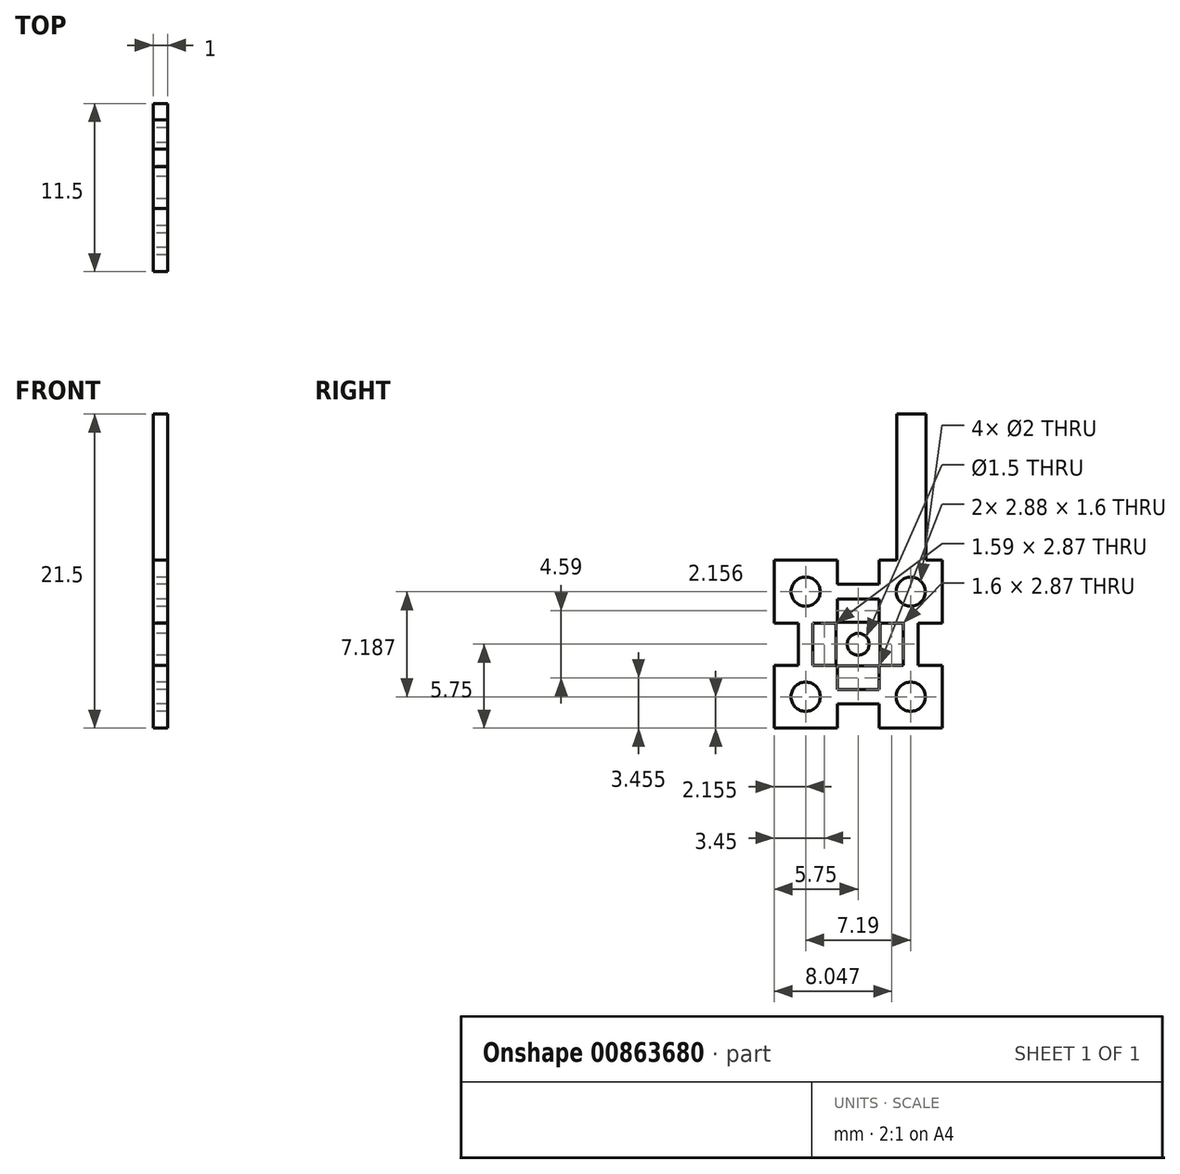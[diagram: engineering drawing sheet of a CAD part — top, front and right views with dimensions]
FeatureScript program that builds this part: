
annotation { "Feature Type Name" : "Feature", "Feature Type Description" : "" }
export const myFeature = defineFeature(function(context is Context, id is Id, definition is map)
    precondition{}
    {
        {
            var Q0;
            Q0=qCreatedBy(makeId("Right.planeOp"),FACE);
            var sketch = newSketch(context, id + "F0", { "sketchPlane" : qUnion([Q0])});
            skLineSegment(sketch, "E0.bottom", {"start": v(0, 0) * mm, "end": v(4.31, 0) * mm});
            skLineSegment(sketch, "E0.top", {"start": v(0, -11.5) * mm, "end": v(4.31, -11.5) * mm});
            skLineSegment(sketch, "E0.left", {"start": v(0, 0) * mm, "end": v(0, -4.31) * mm});
            skLineSegment(sketch, "E1", {"start": v(11.5, 0) * mm, "end": v(11.5, -4.31) * mm});
            skLineSegment(sketch, "E2", {"start": v(10.38, 0) * mm, "end": v(10.38, 10) * mm});
            skLineSegment(sketch, "E3", {"start": v(10.38, 10) * mm, "end": v(8.38, 10) * mm});
            skLineSegment(sketch, "E4", {"start": v(8.38, 10) * mm, "end": v(8.38, 0) * mm});
            skLineSegment(sketch, "E5.trimOffspring", {"start": v(10.38, 0) * mm, "end": v(11.5, 0) * mm});
            skLineSegment(sketch, "E6.0", {"start": v(0, -7.19) * mm, "end": v(4.31, -7.19) * mm});
            skLineSegment(sketch, "E7.0", {"start": v(0, -4.31) * mm, "end": v(4.31, -4.31) * mm});
            skLineSegment(sketch, "E8.0", {"start": v(4.31, 0) * mm, "end": v(4.31, -4.31) * mm});
            skLineSegment(sketch, "E9.0", {"start": v(7.19, 0) * mm, "end": v(7.19, -4.31) * mm});
            skLineSegment(sketch, "E10", {"start": v(8.38, 0) * mm, "end": v(7.19, 0) * mm});
            skLineSegment(sketch, "E11", {"start": v(7.19, 0) * mm, "end": v(8.38, 0) * mm});
            skLineSegment(sketch, "E12.trimOffspring", {"start": v(0, -7.19) * mm, "end": v(0, -11.5) * mm});
            skLineSegment(sketch, "E13.trimOffspring", {"start": v(4.31, -7.19) * mm, "end": v(4.31, -11.5) * mm});
            skLineSegment(sketch, "E14.trimOffspring", {"start": v(7.19, -7.19) * mm, "end": v(7.19, -11.5) * mm});
            skLineSegment(sketch, "E15.trimOffspring", {"start": v(11.5, -7.19) * mm, "end": v(11.5, -11.5) * mm});
            skLineSegment(sketch, "E16.trimOffspring", {"start": v(7.19, -4.31) * mm, "end": v(11.5, -4.31) * mm});
            skLineSegment(sketch, "E17.trimOffspring", {"start": v(7.19, -7.19) * mm, "end": v(11.5, -7.19) * mm});
            skLineSegment(sketch, "E18.trimOffspring", {"start": v(7.19, -11.5) * mm, "end": v(11.5, -11.5) * mm});
            skLineSegment(sketch, "E19.0", {"start": v(4.31, -2.66) * mm, "end": v(7.19, -2.66) * mm});
            skLineSegment(sketch, "E20.0", {"start": v(4.31, -1.66) * mm, "end": v(7.19, -1.66) * mm});
            skLineSegment(sketch, "E21.0", {"start": v(1.66, -4.31) * mm, "end": v(1.66, -7.19) * mm});
            skLineSegment(sketch, "E22.0", {"start": v(2.66, -4.31) * mm, "end": v(2.66, -7.19) * mm});
            skLineSegment(sketch, "E23.0", {"start": v(4.3, -9.84) * mm, "end": v(7.19, -9.84) * mm});
            skLineSegment(sketch, "E24.0", {"start": v(4.31, -8.84) * mm, "end": v(7.19, -8.84) * mm});
            skLineSegment(sketch, "E25.0", {"start": v(8.84, -4.31) * mm, "end": v(8.84, -7.19) * mm});
            skLineSegment(sketch, "E26.0", {"start": v(9.84, -4.31) * mm, "end": v(9.84, -7.19) * mm});
            skPoint(sketch, "E27.end.orphan", {"position": v(7.19, -2.16) * mm});
            skPoint(sketch, "E27.start.orphan", {"position": v(4.31, -2.16) * mm});
            skPoint(sketch, "E28.end.orphan", {"position": v(9.34, -7.19) * mm});
            skPoint(sketch, "E28.start.orphan", {"position": v(9.34, -4.31) * mm});
            skPoint(sketch, "E29.end.orphan", {"position": v(7.19, -9.34) * mm});
            skPoint(sketch, "E29.start.orphan", {"position": v(4.31, -9.34) * mm});
            skPoint(sketch, "E30.end.orphan", {"position": v(2.16, -7.19) * mm});
            skPoint(sketch, "E30.start.orphan", {"position": v(2.16, -4.31) * mm});
            skLineSegment(sketch, "E31", {"start": v(8.38, 0) * mm, "end": v(10.38, 0) * mm});
            skCircle(sketch, "E32", {"center": v(2.16, -9.34) * mm, "radius": 1 * mm});
            skCircle(sketch, "E33", {"center": v(2.16, -2.16) * mm, "radius": 1 * mm});
            skCircle(sketch, "E34", {"center": v(9.34, -2.16) * mm, "radius": 1 * mm});
            skCircle(sketch, "E35", {"center": v(9.34, -9.34) * mm, "radius": 1 * mm});
            skCircle(sketch, "E36", {"center": v(5.75, -5.75) * mm, "radius": 0.75 * mm});
            skPoint(sketch, "E36.centerSnap0", {"position": v(7.19, -5.75) * mm});
            skPoint(sketch, "E36.centerSnap1", {"position": v(5.75, -4.31) * mm});
            skLineSegment(sketch, "E37.0", {"start": v(4.31, -4.25) * mm, "end": v(7.19, -4.25) * mm});
            skLineSegment(sketch, "E38.0", {"start": v(4.31, -7.25) * mm, "end": v(7.19, -7.25) * mm});
            skLineSegment(sketch, "E39.0", {"start": v(4.25, -7.19) * mm, "end": v(4.25, -4.31) * mm});
            skLineSegment(sketch, "E40.0", {"start": v(7.25, -4.31) * mm, "end": v(7.25, -7.19) * mm});
            skSolve(sketch);
        }
        {
            var Q0;
            {var subQ6=sQuery(id+"F0.wireOp",EDGE,"E0.bottom");Q0=makeQuery(id+"F0.imprint","IMPRINT",FACE,{"disambiguationData":[TD([[makeQuery(id+"F0.imprint","IMPRINT",EDGE,{"derivedFrom":subQ6}),-1.0]])]});}
            var Q1;
            {var subQ1=sQuery(id+"F0.wireOp",EDGE,"E1");Q1=makeQuery(id+"F0.imprint","IMPRINT",FACE,{"disambiguationData":[TD([[makeQuery(id+"F0.imprint","IMPRINT",EDGE,{"derivedFrom":subQ1}),-1.0]])]});}
            var Q2;
            {var subQ0=sQuery(id+"F0.wireOp",EDGE,"E19.0");Q2=makeQuery(id+"F0.imprint","IMPRINT",FACE,{"disambiguationData":[TD([[makeQuery(id+"F0.imprint","IMPRINT",EDGE,{"derivedFrom":subQ0}),1.0]])]});}
            var Q3;
            {var subQ0=sQuery(id+"F0.wireOp",EDGE,"E21.0");Q3=makeQuery(id+"F0.imprint","IMPRINT",FACE,{"disambiguationData":[TD([[makeQuery(id+"F0.imprint","IMPRINT",EDGE,{"derivedFrom":subQ0}),1.0]])]});}
            var Q4;
            {var subQ1=sQuery(id+"F0.wireOp",EDGE,"E0.top");Q4=makeQuery(id+"F0.imprint","IMPRINT",FACE,{"disambiguationData":[TD([[makeQuery(id+"F0.imprint","IMPRINT",EDGE,{"derivedFrom":subQ1}),1.0]])]});}
            var Q5;
            {var subQ4=sQuery(id+"F0.wireOp",EDGE,"E15.trimOffspring");Q5=makeQuery(id+"F0.imprint","IMPRINT",FACE,{"disambiguationData":[TD([[makeQuery(id+"F0.imprint","IMPRINT",EDGE,{"derivedFrom":subQ4}),-1.0]])]});}
            var Q6;
            {var subQ0=sQuery(id+"F0.wireOp",EDGE,"E23.0");Q6=makeQuery(id+"F0.imprint","IMPRINT",FACE,{"disambiguationData":[TD([[makeQuery(id+"F0.imprint","IMPRINT",EDGE,{"derivedFrom":subQ0}),1.0]])]});}
            var Q7;
            Q7=makeQuery(id+"F0.imprint","IMPRINT",FACE,{"disambiguationData":[TD([[makeQuery(id+"F0.imprint","IMPRINT",EDGE,{"derivedFrom":sQuery(id+"F0.wireOp",EDGE,"E36")}),-1.0]])]});
            var Q8;
            {var subQ0=sQuery(id+"F0.wireOp",EDGE,"E25.0");Q8=makeQuery(id+"F0.imprint","IMPRINT",FACE,{"disambiguationData":[TD([[makeQuery(id+"F0.imprint","IMPRINT",EDGE,{"derivedFrom":subQ0}),1.0]])]});}
            var Q9;
            Q9=makeQuery(id+"F0.imprint","IMPRINT",FACE,{"disambiguationData":[TD([[makeQuery(id+"F0.imprint","IMPRINT",EDGE,{"derivedFrom":sQuery(id+"F0.wireOp",EDGE,"E2")}),1.0]])]});
            extrude(context, id + "F1", {"entities" : qUnion([Q0, Q1, Q2, Q3, Q4, Q5, Q6, Q7, Q8, Q9]), "depth" : 1 * mm, "offsetDistance" : 25 * mm});
        }
    });
